# Revit family: 14-10 WELDING BOOTH
name_source: partatom
category: Generic Models
revit_build: Autodesk Revit LT 2013 (Build: 20130531_0300(x64)
units: mm (PartAtom-declared; Revit-internal decimal feet)

## types (1)
- 14-10 WELDING BOOTH
    BASE PLATE DEPTH = 100 mm  [stored 0.328084 ft]
    BASE PLATE THICKNESS = 10 mm  [stored 0.0328084 ft]
    BASE PLATE WIDTH = 100 mm  [stored 0.328084 ft]
    BOOTH HEIGHT = 2300 mm
    FLOOR CLEARANCE = 400 mm  [stored 1.31234 ft]
    HOOD HEIGHT = 600 mm
    HOOD THICKNESS = 3 mm  [stored 0.00984252 ft]
    HOOD TOP DEPTH = 500 mm  [stored 1.64042 ft]
    HOOD TOP WIDTH = 500 mm  [stored 1.64042 ft]
    POST DEPTH = 50 mm  [stored 0.164042 ft]
    POST HORIZONTAL DEPTH = 50 mm  [stored 0.164042 ft]
    POST WIDTH = 50 mm  [stored 0.164042 ft]
    WALL PANEL THICKNESS = 10 mm  [stored 0.0328084 ft]

note: [stored X ft] marks values corroborated as IEEE doubles in the binary element streams (Revit-internal decimal feet)

## geometry (parser evidence)
native form markers: Sweep x3
no freeform markers — native parametric forms only
